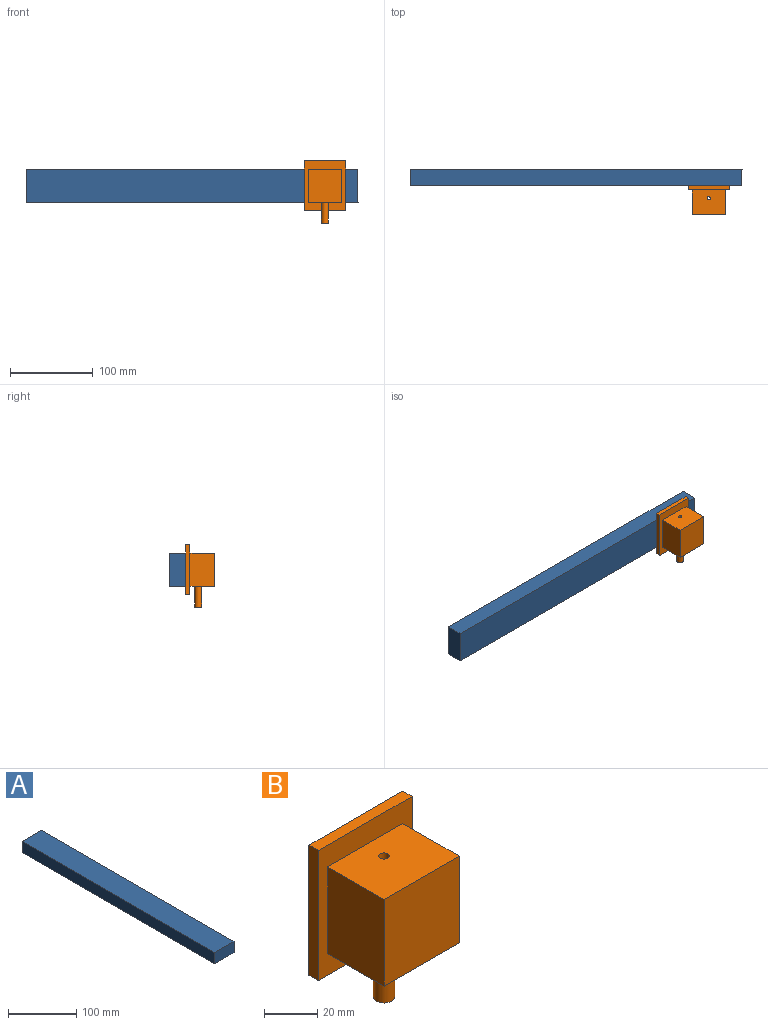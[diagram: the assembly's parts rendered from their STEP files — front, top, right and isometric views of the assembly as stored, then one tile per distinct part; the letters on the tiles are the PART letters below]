
ASSEMBLY  parts=2 mates=1
PART A: 6 faces, bbox 40x400x20 mm
  f0: plane 400x20mm, normal (-1,0,0), area 8000mm2, adj f1,f3,f4,f5
  f1: plane 400x40mm, normal (0,0,-1), area 16000mm2, adj f0,f2,f4,f5
  f2: plane 400x20mm, normal (1,0,0), area 8000mm2, adj f1,f3,f4,f5
  f3: plane 400x40mm, normal (0,0,1), area 16000mm2, adj f0,f2,f4,f5
  f4: plane 40x20mm, normal (0,-1,0), area 800mm2, adj f0,f1,f2,f3
  f5: plane 40x20mm, normal (0,1,0), area 800mm2, adj f0,f1,f2,f3
PART B: 14 faces, bbox 50x35x75 mm
  f0: plane 40x30mm, normal (0,0,-1), area 1149.7mm2, adj f1,f3,f4,f6,f8
  f1: plane 40x30mm, normal (1,0,0), area 1200mm2, adj f0,f2,f4,f8
  f2: plane 40x30mm, normal (0,0,1), area 1187.4mm2, adj f1,f3,f4,f5,f8
  f3: plane 40x30mm, normal (-1,0,0), area 1200mm2, adj f0,f2,f4,f8
  f4: plane 40x40mm, normal (0,-1,0), area 1600mm2, adj f0,f1,f2,f3
  f5: cylinder r=2mm len=65mm, axis (0,0,1), area 816.8mm2, adj f2,f7
  f6: cylinder r=4mm len=25mm, axis (0,0,1), area 628.3mm2, adj f0,f7
  f7: plane 8x8mm, normal (0,0,-1), area 37.7mm2, adj f5,f6
  f8: plane 60x50mm, normal (0,-1,0), area 1400mm2, adj f0,f1,f2,f3,f9,f11,f12,f13
  f9: plane 50x5mm, normal (0,0,-1), area 250mm2, adj f8,f10,f12,f13
  f10: plane 60x50mm, normal (0,1,0), area 3000mm2, adj f9,f11,f12,f13
  f11: plane 50x5mm, normal (0,0,1), area 250mm2, adj f8,f10,f12,f13
  f12: plane 60x5mm, normal (1,0,0), area 300mm2, adj f8,f9,f10,f11
  f13: plane 60x5mm, normal (-1,0,0), area 300mm2, adj f8,f9,f10,f11
PLACE A rot(axis=(-0.58,0.58,0.58),120deg) t=(875.46,-284.48,-8.87)mm
PLACE B rot(axis=(0.92,-0.11,-0.38),0deg) t=(1035.46,-299.48,-8.87)mm
MATE slider A.f5 <-> B.f1  axis (-1,0,0) through (675.46,-294.48,11.13)mm
